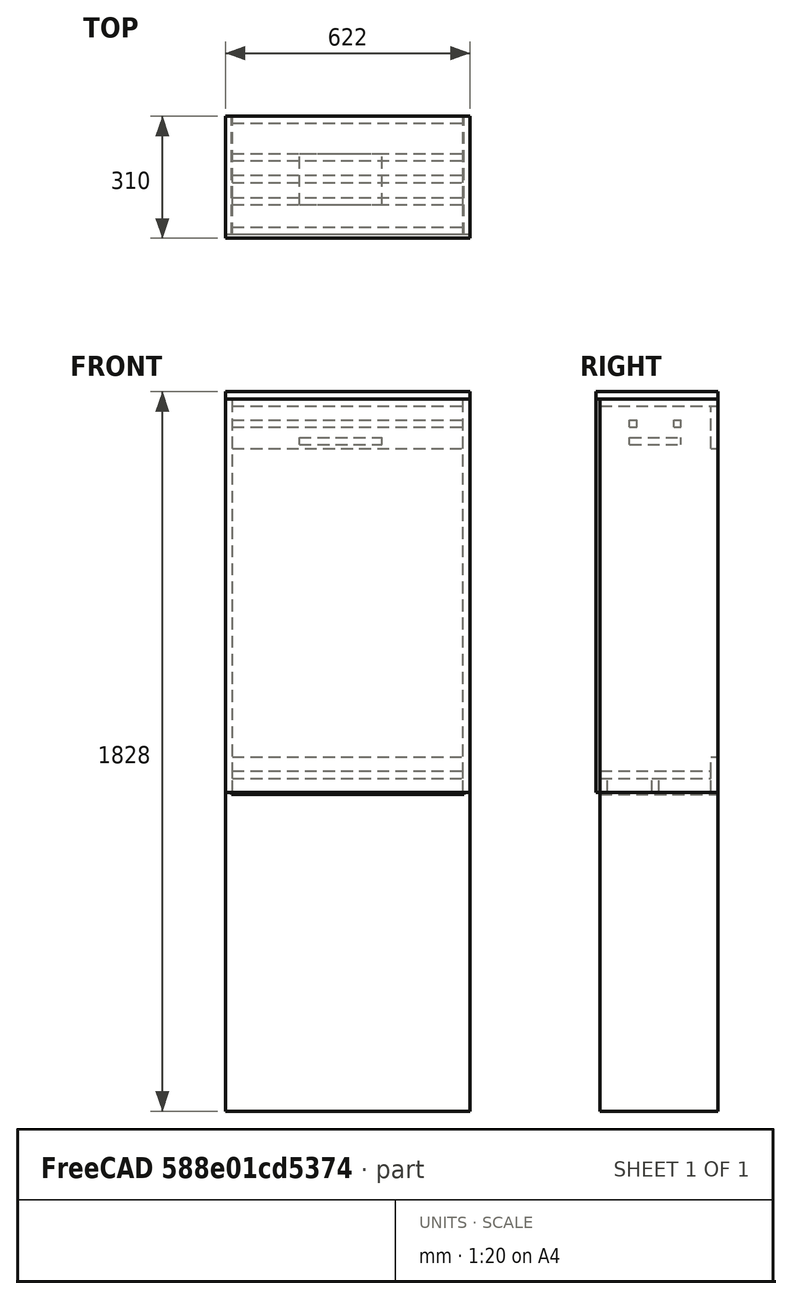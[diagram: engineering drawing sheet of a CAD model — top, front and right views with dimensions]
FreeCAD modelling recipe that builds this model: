
FCSTD DOCUMENT  (FreeCAD 0.21R33771 (Git))
Label: cabinet_freecad
License: All rights reserved
LicenseURL: http://en.wikipedia.org/wiki/All_rights_reserved
objects: Part::Box×16, App::DocumentObjectGroup×3, App::MeasureDistance×3, Part::MultiFuse×1, Part::Feature×1
note: 18 computed .brp shape members not serialized (recipe doc carries the construction recipe); baked Part::Feature solids carry a one-line shape summary decoded from their .brp

FEATURE [Part::Box] cube
  AttacherType = Attacher::AttachEngine3D
  Height = 810
  Length = 16
  Width = 300
FEATURE [Part::Box] cube001
  AttacherType = Attacher::AttachEngine3D
  Height = 810
  Length = 16
  Placement = pos=(606,0,0) rot=(0,0,1;0rad)
  Width = 300
FEATURE [Part::Box] cube002
  AttacherType = Attacher::AttachEngine3D
  Height = 16
  Length = 590
  Placement = pos=(16,0,789) rot=(0,0,1;0rad)
  Width = 300
FEATURE [Part::Box] cube003
  AttacherType = Attacher::AttachEngine3D
  Height = 789
  Length = 590
  Placement = pos=(16,0,0) rot=(0,0,1;0rad)
  Width = 300
FEATURE [Part::MultiFuse] Group  label="base_drawers"
  Shapes = -> [cube,cube001,cube002,cube003]
FEATURE [Part::Box] cube004  label="sidepanel_r"
  AttacherType = Attacher::AttachEngine3D
  Height = 1000
  Length = 18
  Placement = pos=(0,0,810) rot=(0,0,1;0rad)
  Width = 300
FEATURE [Part::Box] cube005  label="sidepanel_l"
  AttacherType = Attacher::AttachEngine3D
  Height = 1000
  Length = 18
  Placement = pos=(604,0,810) rot=(0,0,1;0rad)
  Width = 300
FEATURE [Part::Box] cube006  label="toppanel"
  AttacherType = Attacher::AttachEngine3D
  Height = 18
  Length = 586
  Placement = pos=(18,0,1792) rot=(0,0,1;0rad)
  Width = 300
FEATURE [Part::Box] cube007  label="backboard"
  AttacherType = Attacher::AttachEngine3D
  Height = 1000
  Length = 622
  Placement = pos=(0,-10,810) rot=(0,0,1;0rad)
  Width = 10
FEATURE [Part::Feature] Group001_solid  label="cabinet_wip (Solid)"
  shape: bbox 622 x 310 x 1018 mm, 19 faces (baked)
FEATURE [Part::Box] cube008  label="base"
  AttacherType = Attacher::AttachEngine3D
  Height = 18
  Length = 586
  Placement = pos=(18,0,846) rot=(0,0,1;0rad)
  Width = 282
FEATURE [Part::Box] cube009  label="bottompanel_support_back"
  AttacherType = Attacher::AttachEngine3D
  Height = 36
  Length = 586
  Placement = pos=(18,0,810) rot=(0,0,1;0rad)
  Width = 18
FEATURE [Part::Box] cube010  label="toppanel_shade"
  AttacherType = Attacher::AttachEngine3D
  Height = 108
  Length = 586
  Placement = pos=(18,282,1684) rot=(0,0,1;0rad)
  Width = 18
FEATURE [Part::Box] cube011  label="frontpanel"
  AttacherType = Attacher::AttachEngine3D
  Height = 90
  Length = 586
  Placement = pos=(18,282,810) rot=(0,0,1;0rad)
  Width = 18
FEATURE [App::DocumentObjectGroup] Group002  label="toppanel001"
  Group = -> [cube010,cube006]
FEATURE [App::MeasureDistance] Distance  label="Distance: 264.40 mm"
  Distance = 264.4
  P1 = (604,18,810)
  P2 = (604,282.4,810)
FEATURE [Part::Box] cube012  label="bottompanel_support_middle"
  AttacherType = Attacher::AttachEngine3D
  Height = 36
  Length = 586
  Placement = pos=(18,132,810) rot=(0,0,1;0rad)
  Width = 18
FEATURE [App::DocumentObjectGroup] Group001  label="bottompanel001"
  Group = -> [cube008,cube011,cube009,cube012]
FEATURE [Part::Box] cube013  label="led_lamp"
  AttacherType = Attacher::AttachEngine3D
  Height = 18
  Length = 210
  Placement = pos=(188,75,1694) rot=(0,0,1;0rad)
  Width = 130
FEATURE [App::MeasureDistance] Distance001  label="Distance: 586.00 mm"
  Distance = 586
  P1 = (604,300,1810)
  P2 = (18,300,1810)
FEATURE [App::MeasureDistance] Distance002  label="Distance: 946.00 mm"
  Distance = 946
  P1 = (18.414,0.355624,864)
  P2 = (18,0.208291,1810)
FEATURE [Part::Box] cube014  label="support_beam"
  AttacherType = Attacher::AttachEngine3D
  Height = 18
  Length = 586
  Placement = pos=(18,75,1738) rot=(0,0,1;0rad)
  Width = 18
FEATURE [Part::Box] cube015  label="support_beam_front"
  AttacherType = Attacher::AttachEngine3D
  Height = 18
  Length = 586
  Placement = pos=(18,187,1738) rot=(0,0,1;0rad)
  Width = 18
FEATURE [App::DocumentObjectGroup] Group003  label="light_setup"
  Group = -> [cube013,cube015]
